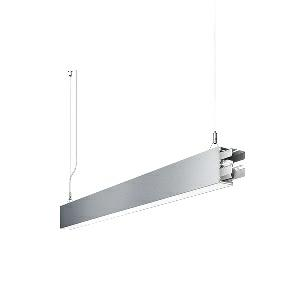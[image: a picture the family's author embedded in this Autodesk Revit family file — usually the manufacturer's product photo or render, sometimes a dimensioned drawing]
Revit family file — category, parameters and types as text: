
# Revit family: dotoo_line_-_dlp_1500_840_d_sta_00805822_c6be
name_source: partatom
category: Lighting Fixtures
units: mm (PartAtom-declared; Revit-internal decimal feet)

## family parameters
Cut with Voids When Loaded = No
Host = Face
Light Source = No
Part Type = Normal
Room Calculation Point = No
Round Connector Dimension = Use Diameter
Shared = No

## types (1)
- DOTOO.line - DLP 1500/840/D STA (1 x LED, 1350 lm, 4000K)
    Apparent Load = 13 VA
    Approval mark = CE
    CIE Flux Codes = 67 91 98 100 100
    Color Rendering = 80-89
    Color Temperature = 4000K
    Control Gear = Electronic ballast
    Default Elevation = 1800 mm
    Description = DLP 1500/840/D|Suspended luminaire|light source: LED|connected load: 220-240 V, 50/60 Hz|Power consumption: approx. 13 W|standby: approx. 0,20|luminous flux: 1350 lm|luminous efficacy: 103 lm/W|light distribution: Direct|direct ratio: approx. 100 %|colour temperature: Cold white, ca. 4000 K|color rendering index (CRI): >= 80|chromaticity tolerance:  3 SDCM|System of protection: IP 40|technology: Continuously dimmable|luminaire body|material: Sectional aluminium|colour: Silver|lamp cover: Acrylic (PMMA), Clear|mains lead: 2.00 m With free stranded wires|Fastening: Steel cable 0.3 - 0.7 m|glare control: Prism aperture|luminance(L65): <= 3000 cd/m|unified glare rating(4H 8H): <=  19|special features: DALI Load 1x, TouchDIM - dimming via standard switch, Through-wired, up to 18 m on one mains connection, Flicker-free, Suitable as emergency lighting, Start luminaire with mains connection, Mechanical and electrical connection of the individual modules without tools|
    Frequency = 50 Hz
    Height = 110 mm
    Lamp = 1 x LED
    Lamp Light Flux = 1350 lm
    Lamp count = 1
    Length = 1128 mm
    Luminous efficacy = 104 lm/W
    Manufacturer = Waldmann
    ModVariant = No
    Model = 00805822
    Mounting Place = Ceiling
    Mounting Type = Pendant
    Number of Poles = 1
    OnlyDefault = Yes
    Power Factor = 1
    Product Name = DOTOO.line - DLP 1500/840/D STA
    Product group = Suspended luminaire
    ProductGroupID = 9
    Protection Class = Protection class I
    Protection Degree = IP 40
    RLX_Detail_Level = 1
    RLX_Emergency_Light_Flux = 0 lm
    RLX_Emergency_Type = 0
    RLX_Emergency_Type_DB = No
    RlxData = <blob elided: 22501 chars, md5=581b7e45>
    Socket = socket
    Standby Power = 0 W
    System Light Flux = 1350 lm
    System Power = 13 W
    Type Comments = Product without accessories
    Type Image = 113304000-00692576.jpg
    URL = http://relux.com
    VarID = ---
    Voltage = 230 V
    Voltage Range = 220-240 V
    Weight = 0.00 kg
    Width = 60 mm  [stored 0.19685 ft]

note: [stored X ft] marks values corroborated as IEEE doubles in the binary element streams (Revit-internal decimal feet)

## geometry (parser evidence)
native form markers: Blend x4, Sweep x12
no freeform markers — native parametric forms only
